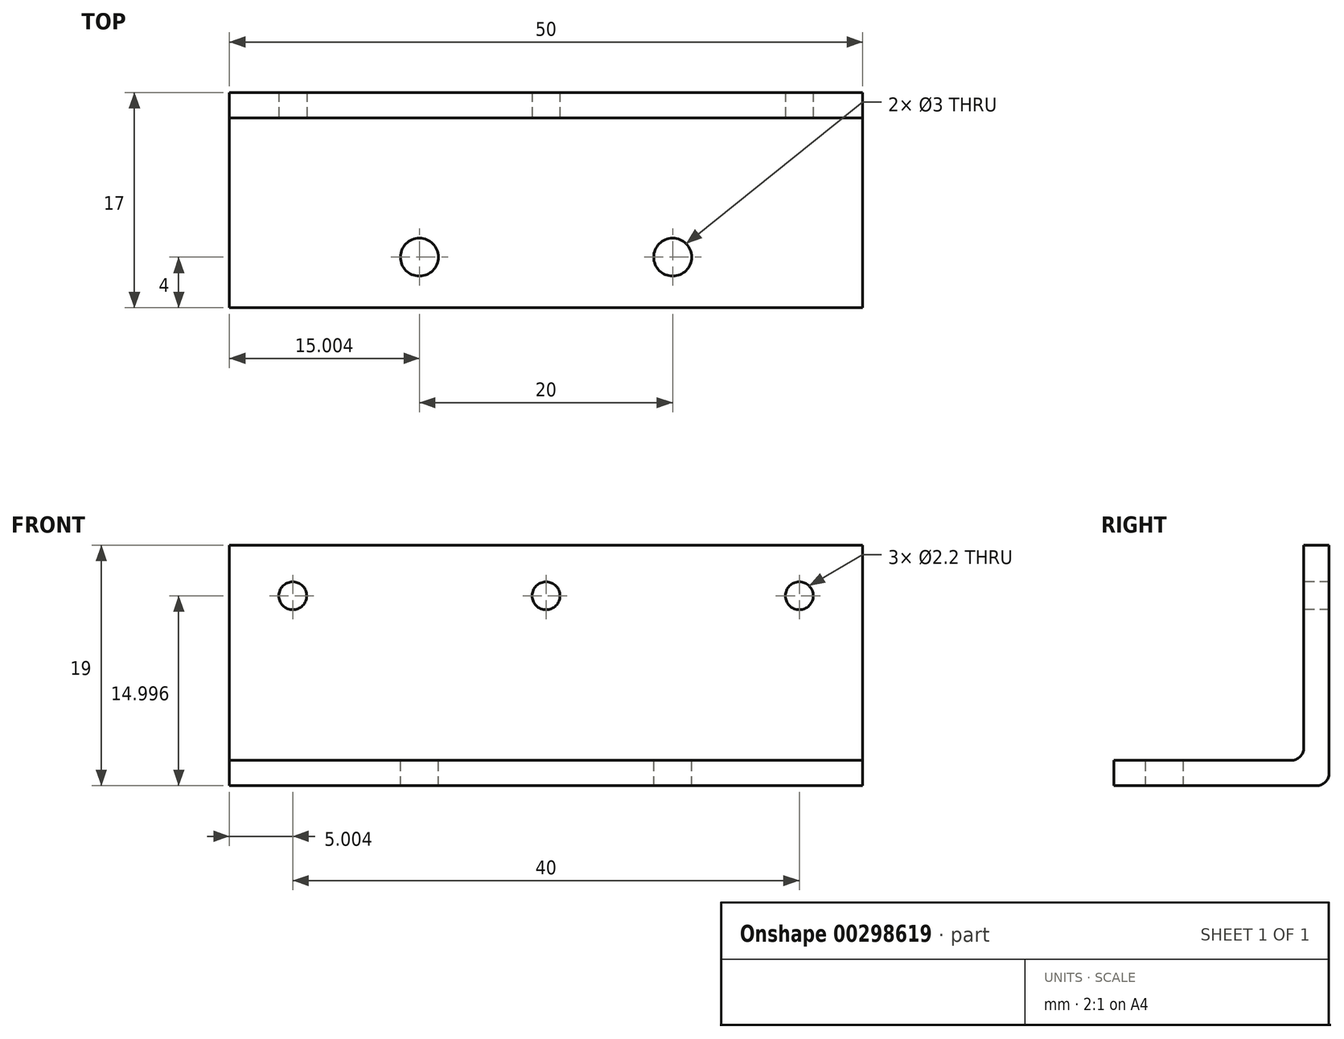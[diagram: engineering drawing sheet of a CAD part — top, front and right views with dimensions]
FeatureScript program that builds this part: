
annotation { "Feature Type Name" : "Feature", "Feature Type Description" : "" }
export const myFeature = defineFeature(function(context is Context, id is Id, definition is map)
    precondition{}
    {
        {
            var Q0;
            Q0=qCreatedBy(makeId("Front.planeOp"),FACE);
            var sketch = newSketch(context, id + "F0", { "sketchPlane" : qUnion([Q0])});
            skLineSegment(sketch, "E0.bottom", {"start": v(-55, 57.07) * mm, "end": v(-53, 57.07) * mm});
            skLineSegment(sketch, "E0.left", {"start": v(-55, 57.07) * mm, "end": v(-55, 38.07) * mm});
            skLineSegment(sketch, "E0.right", {"start": v(-53, 57.07) * mm, "end": v(-53, 40.07) * mm});
            skLineSegment(sketch, "E1.bottom", {"start": v(-55, 38.07) * mm, "end": v(-38, 38.07) * mm});
            skLineSegment(sketch, "E1.top", {"start": v(-53, 40.07) * mm, "end": v(-38, 40.07) * mm});
            skLineSegment(sketch, "E1.right", {"start": v(-38, 38.07) * mm, "end": v(-38, 40.07) * mm});
            skSolve(sketch);
        }
        {
            var Q0;
            Q0=qSketchRegion(id+"F0",true);
            extrude(context, id + "F1", {"entities" : qUnion([Q0]), "depth" : 50 * mm});
        }
        {
            var Q0;
            Q0=makeQuery(id+"F1.opExtrude","SWEPT_FACE",FACE,{"disambiguationData":[OSD([sQuery(id+"F0.wireOp",EDGE,"E0.right")])]});
            var sketch = newSketch(context, id + "F2", { "sketchPlane" : qUnion([Q0])});
            skCircle(sketch, "E2", {"center": v(-45, 53.07) * mm, "radius": 1.1 * mm});
            skCircle(sketch, "E3", {"center": v(-5, 53.07) * mm, "radius": 1.1 * mm});
            skCircle(sketch, "E4", {"center": v(-25, 53.07) * mm, "radius": 1.1 * mm});
            skPoint(sketch, "E4.centerSnap0", {"position": v(-25, 57.07) * mm});
            skSolve(sketch);
        }
        {
            var Q0;
            Q0=qSketchRegion(id+"F2",true);
            extrude(context, id + "F3", {"entities" : qUnion([Q0]), "operationType" : NewBodyOperationType.REMOVE, "oppositeDirection" : true, "depth" : 2 * mm});
        }
        {
            var Q0;
            Q0=makeQuery(id+"F1.opExtrude","SWEPT_FACE",FACE,{"disambiguationData":[OSD([sQuery(id+"F0.wireOp",EDGE,"E1.top")])]});
            var sketch = newSketch(context, id + "F4", { "sketchPlane" : qUnion([Q0])});
            skCircle(sketch, "E5", {"center": v(-42, -35) * mm, "radius": 1.5 * mm});
            skCircle(sketch, "E6", {"center": v(-42, -15) * mm, "radius": 1.5 * mm});
            skSolve(sketch);
        }
        {
            var Q0;
            Q0=qSketchRegion(id+"F4",true);
            extrude(context, id + "F5", {"entities" : qUnion([Q0]), "operationType" : NewBodyOperationType.REMOVE, "oppositeDirection" : true, "depth" : 2 * mm});
        }
        {
            var Q0;
            Q0=makeQuery(id+"F1.opExtrude","SWEPT_EDGE",EDGE,{"disambiguationData":[OSD([sQuery(id+"F0.wireOp",EDGE,"E0.right"),sQuery(id+"F0.wireOp",EDGE,"E1.top")])]});
            var Q1;
            Q1=makeQuery(id+"F1.opExtrude","SWEPT_EDGE",EDGE,{"disambiguationData":[OSD([sQuery(id+"F0.wireOp",EDGE,"E0.left"),sQuery(id+"F0.wireOp",EDGE,"E1.bottom")])]});
            fillet(context, id + "F6", {"entities" : qUnion([Q0, Q1]), "radius" : 1 * mm, "tangentPropagation" : true, "allowEdgeOverflow" : false});
        }
        {
            var Q0;
            Q0=makeQuery(id+"F1.opExtrude","SWEPT_BODY",BODY,{"disambiguationData":[OSD([sQuery(id+"F0.wireOp",EDGE,"E0.bottom"),sQuery(id+"F0.wireOp",EDGE,"E0.left"),sQuery(id+"F0.wireOp",EDGE,"E0.right"),sQuery(id+"F0.wireOp",EDGE,"E1.bottom"),sQuery(id+"F0.wireOp",EDGE,"E1.top"),sQuery(id+"F0.wireOp",EDGE,"E1.right")])]});
            var Q1;
            Q1=makeQuery(id+"F1.opExtrude","CAP_EDGE",EDGE,{"disambiguationData":[OSD([sQuery(id+"F0.wireOp",EDGE,"E0.left")])],"isStart":false});
            transform(context, id + "F7", {"entities" : qUnion([Q0]), "transformType" : TransformType.ROTATION, "transformAxis" : qUnion([Q1]), "angle" : 90 * degree, "makeCopy" : false});
        }
    });
